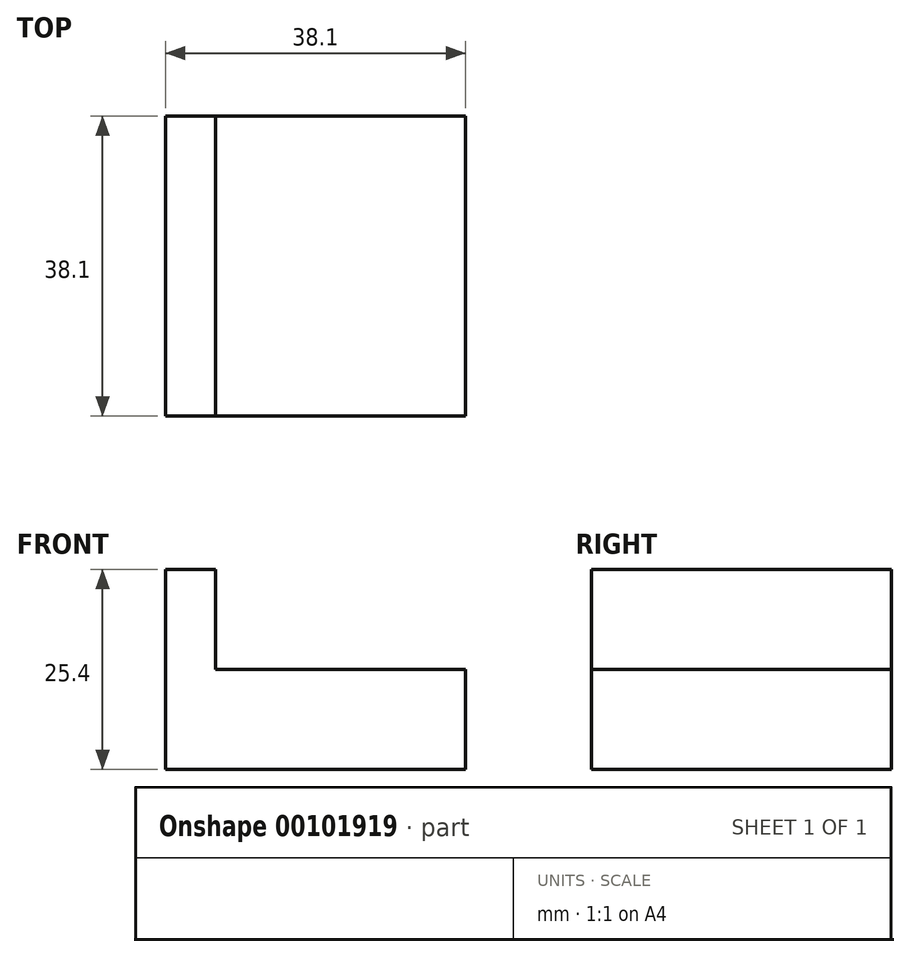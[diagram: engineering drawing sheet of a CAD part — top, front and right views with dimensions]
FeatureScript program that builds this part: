
annotation { "Feature Type Name" : "Feature", "Feature Type Description" : "" }
export const myFeature = defineFeature(function(context is Context, id is Id, definition is map)
    precondition{}
    {
        {
            var Q0;
            Q0=qCreatedBy(makeId("Front.planeOp"),FACE);
            var sketch = newSketch(context, id + "F0", { "sketchPlane" : qUnion([Q0])});
            skLineSegment(sketch, "E0.bottom", {"start": v(0, 0) * mm, "end": v(38.1, 0) * mm});
            skLineSegment(sketch, "E0.top", {"start": v(0, 25.4) * mm, "end": v(38.1, 25.4) * mm});
            skLineSegment(sketch, "E0.left", {"start": v(0, 0) * mm, "end": v(0, 25.4) * mm});
            skLineSegment(sketch, "E0.right", {"start": v(38.1, 0) * mm, "end": v(38.1, 25.4) * mm});
            skLineSegment(sketch, "E1", {"start": v(38.1, 12.7) * mm, "end": v(18.47, 12.7) * mm});
            skSolve(sketch);
        }
        {
            var Q0;
            Q0=makeQuery(id+"F0.imprint","IMPRINT",FACE,{"disambiguationData":[TD([[makeQuery(id+"F0.imprint","IMPRINT",EDGE,{"derivedFrom":sQuery(id+"F0.wireOp",EDGE,"E0.bottom")}),1.0]])]});
            extrude(context, id + "F1", {"entities" : qUnion([Q0]), "depth" : 38.1 * mm});
        }
        {
            var Q0;
            Q0=qCreatedBy(makeId("Front.planeOp"),FACE);
            var sketch = newSketch(context, id + "F2", { "sketchPlane" : qUnion([Q0])});
            skLineSegment(sketch, "E2.top", {"start": v(6.35, 12.7) * mm, "end": v(38.1, 12.7) * mm});
            skLineSegment(sketch, "E3", {"start": v(6.35, 12.7) * mm, "end": v(6.35, 25.4) * mm});
            skLineSegment(sketch, "E4", {"start": v(6.35, 25.4) * mm, "end": v(38.1, 25.4) * mm});
            skLineSegment(sketch, "E5", {"start": v(38.1, 12.7) * mm, "end": v(38.1, 25.4) * mm});
            skSolve(sketch);
        }
        {
            var Q0;
            Q0 = qSketchRegion(id + "F2", true);
            extrude(context, id + "F3", {"entities" : qUnion([Q0]), "operationType" : NewBodyOperationType.REMOVE, "endBound" : BoundingType.SYMMETRIC, "depth" : 106.45 * mm});
        }
    });
